# Revit family: URA Eclairage de Séurité_Bloc a Phare-SATI
name_source: partatom
category: Luminaires
units: mm (PartAtom-declared; Revit-internal decimal feet)

## family parameters
Cote de connecteur circulaire = Utiliser le diamètre
Couper avec des vides une fois chargée = Non
Hôte = Face
Partagée = Non
Repere pour localisation dans la piece = Non
Source d'éclairage = Non
Type d'élément = Normal

## types (4) — shared parameters
Alimentation de secours = Autonome (batterie individuelle)
Autonomie = 1 H
Classe ETIM = EC001957-Luminaire d'éclairage de sécurité
Classe de protection = II
Conditions Générale d'Utilisation = https://export.legrand.com
Consommation en veille = 0 A
Couleur = Noir
Elévation par défaut = 2300 mm
Fabricant = URA
Fonction = Éclairage d'évacuation et d'ambiance
Fréquence = 50/60 Hz
Hauteur = 94 mm
IK = 07
IP = 65
Matière = Plastique
Mode de pose = Montage en saillie (mur)
Objet Connecté = Non
Puissance du système = 1 W
Système de contrôle = Auto-test automatique
Temperature d'utilisation MIN-MAX = 0°C +35°C
Tension = 230 VAC
Type de commutation = Non permanent
Type de connexion = autre
Type de pictogramme = autre
capacité des bornes = 1,5-2,5 mm2
source lumineuse = LED non interchangeable
état des accus = Lithium-ion

## per-type parameters (varying)
| type | 1 phare | 2 phares | Adressable | Batterie de rechange | Code EAN | Description Produit | Flux lumineux utile | Large | Largeur | Long | Longueur | Référence / Modèle |
| BAP Sati Adressable 1000 lm | Oui | Non | Oui | UR111923 | 3613400171347 | BAES 1 PHARE LEDS IP65 1000 LM 1H EVACUATION / AMBIANCE SATI ADRESSABLE | 1000 lm | 137 mm  [stored 0.449475 ft] | 137 mm  [stored 0.449475 ft] | 409 mm | 409 mm | UR130036 |
| BAP Sati Connectable 2500 lm | Non | Oui | Non | 2 x UR111924 | 3613400171361 | BAES 2 PHARES LEDS IP65 2500 LM 1H EVACUATION / AMBIANCE SATI CONNECTABLE | 2500 lm | 240 mm  [stored 0.787402 ft] | 240 mm  [stored 0.787402 ft] | 286 mm | 286 mm | UR130038 |
| BAP Sati Adressable 2500 lm | Non | Oui | Oui | 2 x UR111924 | 3613400171378 | BAES 2 PHARES LEDS IP65 2500 LM 1H EVACUATION / AMBIANCE SATI ADRESSABLE | 2500 lm | 240 mm  [stored 0.787402 ft] | 240 mm  [stored 0.787402 ft] | 286 mm | 286 mm | UR130039 |
| BAP Sati 1H | Non | Oui | Non | 2 x UR111923 | 3613400171354 | BAES 2 PHARES LEDS IP65 2000 LM 1H EVACUATION / AMBIANCE SATI | 2000 lm | 240 mm  [stored 0.787402 ft] | 240 mm  [stored 0.787402 ft] | 286 mm | 286 mm | UR130037 |

note: [stored X ft] marks values corroborated as IEEE doubles in the binary element streams (Revit-internal decimal feet)
